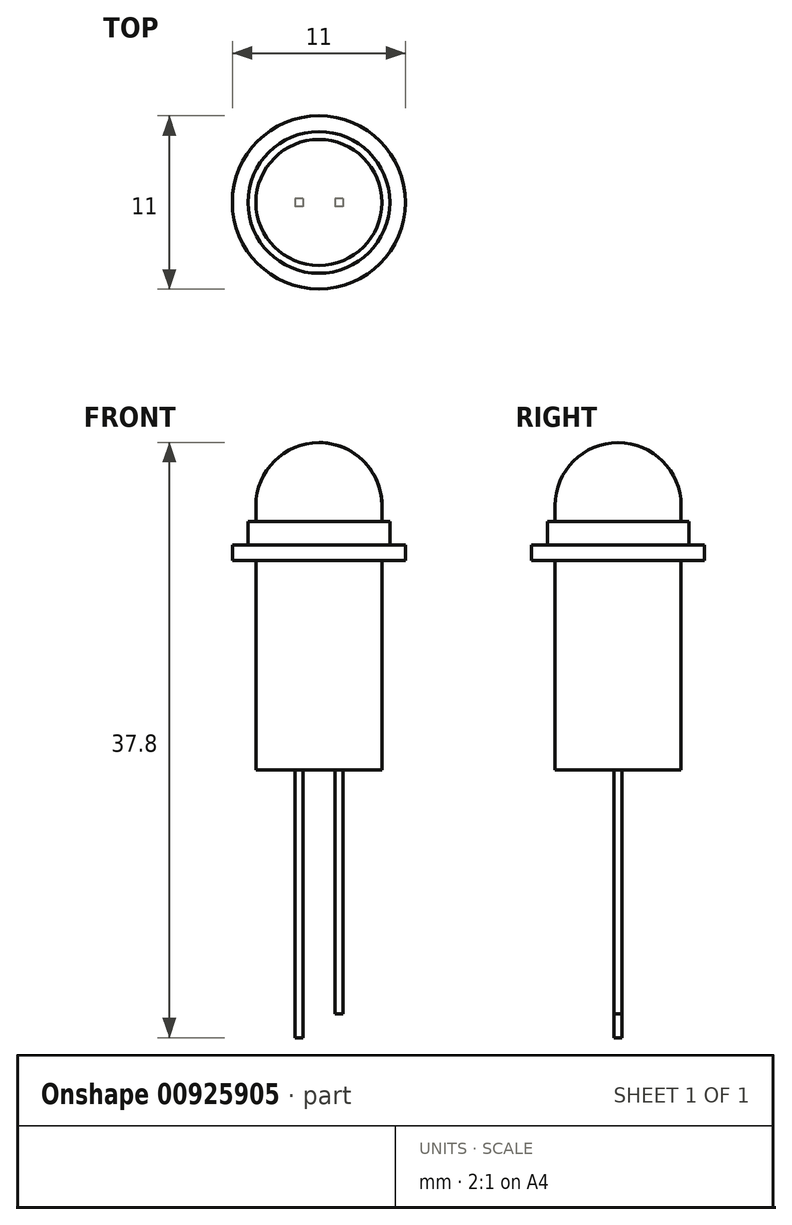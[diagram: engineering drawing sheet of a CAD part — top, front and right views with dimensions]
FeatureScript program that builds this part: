
annotation { "Feature Type Name" : "Feature", "Feature Type Description" : "" }
export const myFeature = defineFeature(function(context is Context, id is Id, definition is map)
    precondition{}
    {
        {
            var Q0;
            Q0=qCreatedBy(makeId("Top.planeOp"),FACE);
            var sketch = newSketch(context, id + "F0", { "sketchPlane" : qUnion([Q0])});
            skCircle(sketch, "E0", {"center": v(0, 0) * mm, "radius": 5.5 * mm});
            skSolve(sketch);
        }
        {
            var Q0;
            Q0 = qSketchRegion(id + "F0", true);
            extrude(context, id + "F1", {"entities" : qUnion([Q0]), "depth" : 1 * mm, "offsetDistance" : 25 * mm});
        }
        {
            var Q0;
            Q0=makeQuery(id+"F1.opExtrude","CAP_FACE",FACE,{"disambiguationData":[OSD([sQuery(id+"F0.wireOp",EDGE,"E0")])],"isStart":false});
            var sketch = newSketch(context, id + "F2", { "sketchPlane" : qUnion([Q0])});
            skCircle(sketch, "E1", {"center": v(0, 0) * mm, "radius": 4.5 * mm});
            skSolve(sketch);
        }
        {
            var Q0;
            Q0 = qSketchRegion(id + "F2", true);
            extrude(context, id + "F3", {"entities" : qUnion([Q0]), "operationType" : NewBodyOperationType.ADD, "depth" : 1.5 * mm, "offsetDistance" : 25 * mm});
        }
        {
            var Q0;
            Q0=makeQuery(id+"F3.opExtrude","CAP_FACE",FACE,{"disambiguationData":[OSD([sQuery(id+"F2.wireOp",EDGE,"E1")])],"isStart":false});
            var sketch = newSketch(context, id + "F4", { "sketchPlane" : qUnion([Q0])});
            skCircle(sketch, "E2", {"center": v(0, 0) * mm, "radius": 4 * mm});
            skSolve(sketch);
        }
        {
            var Q0;
            Q0 = qSketchRegion(id + "F4", true);
            extrude(context, id + "F5", {"entities" : qUnion([Q0]), "operationType" : NewBodyOperationType.ADD, "depth" : 5 * mm, "offsetDistance" : 25 * mm});
        }
        {
            var Q0;
            Q0=makeQuery(id+"F5.opExtrude","CAP_EDGE",EDGE,{"disambiguationData":[OSD([sQuery(id+"F4.wireOp",EDGE,"E2")])],"isStart":false});
            fillet(context, id + "F6", {"entities" : qUnion([Q0]), "radius" : 4 * mm, "tangentPropagation" : true, "allowEdgeOverflow" : false});
        }
        {
            var Q0;
            Q0=makeQuery(id+"F1.opExtrude","CAP_FACE",FACE,{"disambiguationData":[OSD([sQuery(id+"F0.wireOp",EDGE,"E0")])],"isStart":true});
            var sketch = newSketch(context, id + "F7", { "sketchPlane" : qUnion([Q0])});
            skCircle(sketch, "E3", {"center": v(0, 0) * mm, "radius": 4 * mm});
            skSolve(sketch);
        }
        {
            var Q0;
            Q0 = qSketchRegion(id + "F7", true);
            extrude(context, id + "F8", {"entities" : qUnion([Q0]), "operationType" : NewBodyOperationType.ADD, "depth" : 13.3 * mm, "offsetDistance" : 25 * mm});
        }
        {
            var Q0;
            Q0=makeQuery(id+"F8.opExtrude","CAP_FACE",FACE,{"disambiguationData":[OSD([sQuery(id+"F7.wireOp",EDGE,"E3")])],"isStart":false});
            var sketch = newSketch(context, id + "F9", { "sketchPlane" : qUnion([Q0])});
            skLineSegment(sketch, "E4.bottom", {"start": v(-1.02, -0.25) * mm, "end": v(-1.52, -0.25) * mm});
            skLineSegment(sketch, "E4.top", {"start": v(-1.02, 0.25) * mm, "end": v(-1.52, 0.25) * mm});
            skLineSegment(sketch, "E4.left", {"start": v(-1.02, -0.25) * mm, "end": v(-1.02, 0.25) * mm});
            skLineSegment(sketch, "E4.right", {"start": v(-1.52, -0.25) * mm, "end": v(-1.52, 0.25) * mm});
            skPoint(sketch, "E4.middle", {"position": v(-1.27, 0) * mm});
            skLineSegment(sketch, "E5.bottom", {"start": v(1.52, -0.25) * mm, "end": v(1.02, -0.25) * mm});
            skLineSegment(sketch, "E5.top", {"start": v(1.52, 0.25) * mm, "end": v(1.02, 0.25) * mm});
            skLineSegment(sketch, "E5.left", {"start": v(1.52, -0.25) * mm, "end": v(1.52, 0.25) * mm});
            skLineSegment(sketch, "E5.right", {"start": v(1.02, -0.25) * mm, "end": v(1.02, 0.25) * mm});
            skPoint(sketch, "E5.middle", {"position": v(1.27, 0) * mm});
            skSolve(sketch);
        }
        {
            var Q0;
            Q0 = qSketchRegion(id + "F9", true);
            extrude(context, id + "F10", {"entities" : qUnion([Q0]), "operationType" : NewBodyOperationType.ADD, "depth" : 15.5 * mm, "offsetDistance" : 25 * mm});
        }
        {
            var Q0;
            Q0=makeQuery(id+"F10.opExtrude","CAP_FACE",FACE,{"disambiguationData":[OSD([sQuery(id+"F9.wireOp",EDGE,"E4.bottom"),sQuery(id+"F9.wireOp",EDGE,"E4.top"),sQuery(id+"F9.wireOp",EDGE,"E4.left"),sQuery(id+"F9.wireOp",EDGE,"E4.right")])],"isStart":false});
            var sketch = newSketch(context, id + "F11", { "sketchPlane" : qUnion([Q0])});
            skLineSegment(sketch, "E6.bottom", {"start": v(-1.02, -0.25) * mm, "end": v(-1.52, -0.25) * mm});
            skLineSegment(sketch, "E6.top", {"start": v(-1.02, 0.25) * mm, "end": v(-1.52, 0.25) * mm});
            skLineSegment(sketch, "E6.left", {"start": v(-1.02, -0.25) * mm, "end": v(-1.02, 0.25) * mm});
            skLineSegment(sketch, "E6.right", {"start": v(-1.52, -0.25) * mm, "end": v(-1.52, 0.25) * mm});
            skPoint(sketch, "E6.middle", {"position": v(-1.27, 0) * mm});
            skPoint(sketch, "E6.middle.positionSnap0", {"position": v(-1.27, -0.25) * mm});
            skPoint(sketch, "E6.centerSnap0", {"position": v(-1.27, -0.25) * mm});
            skSolve(sketch);
        }
        {
            var Q0;
            Q0 = qSketchRegion(id + "F11", true);
            extrude(context, id + "F12", {"entities" : qUnion([Q0]), "operationType" : NewBodyOperationType.ADD, "depth" : 1.5 * mm, "offsetDistance" : 25 * mm});
        }
    });
